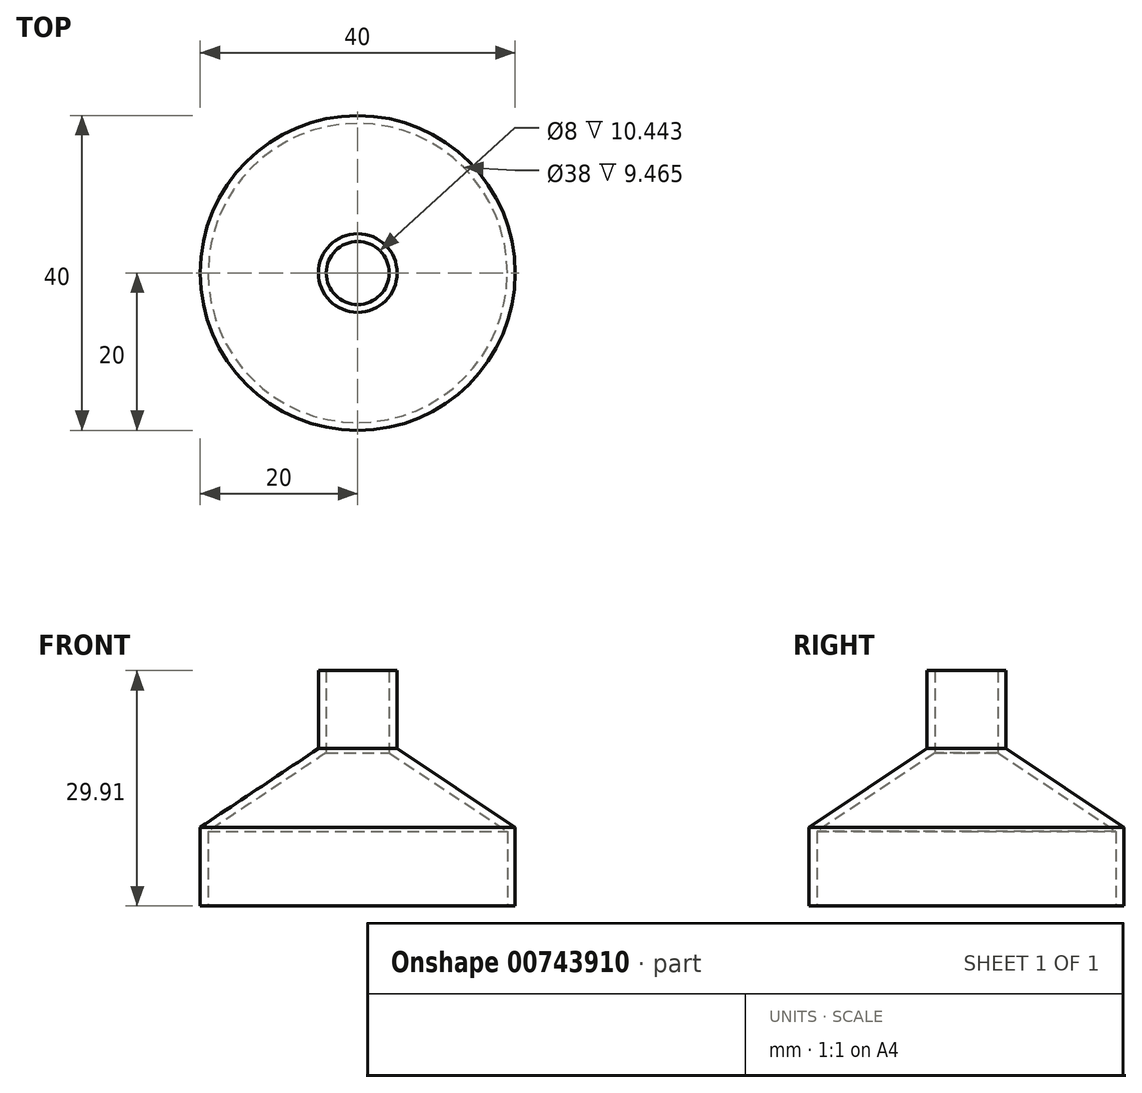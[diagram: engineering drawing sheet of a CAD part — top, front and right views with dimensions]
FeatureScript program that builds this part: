
annotation { "Feature Type Name" : "Feature", "Feature Type Description" : "" }
export const myFeature = defineFeature(function(context is Context, id is Id, definition is map)
    precondition{}
    {
        {
            var Q0;
            Q0=qCreatedBy(makeId("Front.planeOp"),FACE);
            var sketch = newSketch(context, id + "F0", { "sketchPlane" : qUnion([Q0])});
            skLineSegment(sketch, "E0.right", {"start": v(20, 0) * mm, "end": v(20, 10) * mm});
            skLineSegment(sketch, "E1", {"start": v(20, 10) * mm, "end": v(5, 20) * mm});
            skLineSegment(sketch, "E2", {"start": v(5, 20) * mm, "end": v(5, 29.9) * mm});
            skLineSegment(sketch, "E3.0", {"start": v(4, 19.46) * mm, "end": v(4, 29.9) * mm});
            skLineSegment(sketch, "E3.1", {"start": v(19, 9.46) * mm, "end": v(4, 19.46) * mm});
            skLineSegment(sketch, "E4", {"start": v(4, 29.9) * mm, "end": v(5, 29.9) * mm});
            skLineSegment(sketch, "E5", {"start": v(19, 9.46) * mm, "end": v(19, 0) * mm});
            skLineSegment(sketch, "E6", {"start": v(19, 0) * mm, "end": v(20, 0) * mm});
            skLineSegment(sketch, "E7", {"start": v(0, 0) * mm, "end": v(0, 29.86) * mm});
            skSolve(sketch);
        }
        {
            var Q0;
            Q0 = qSketchRegion(id + "F0", true);
            var Q1;
            Q1=sQuery(id+"F0.wireOp",EDGE,"E7");
            revolve(context, id + "F1", {"surfaceOperationType" : NewSurfaceOperationType.NEW, "entities" : qUnion([Q0]), "axis" : qUnion([Q1]), "revolveType" : RevolveType.FULL});
        }
    });
